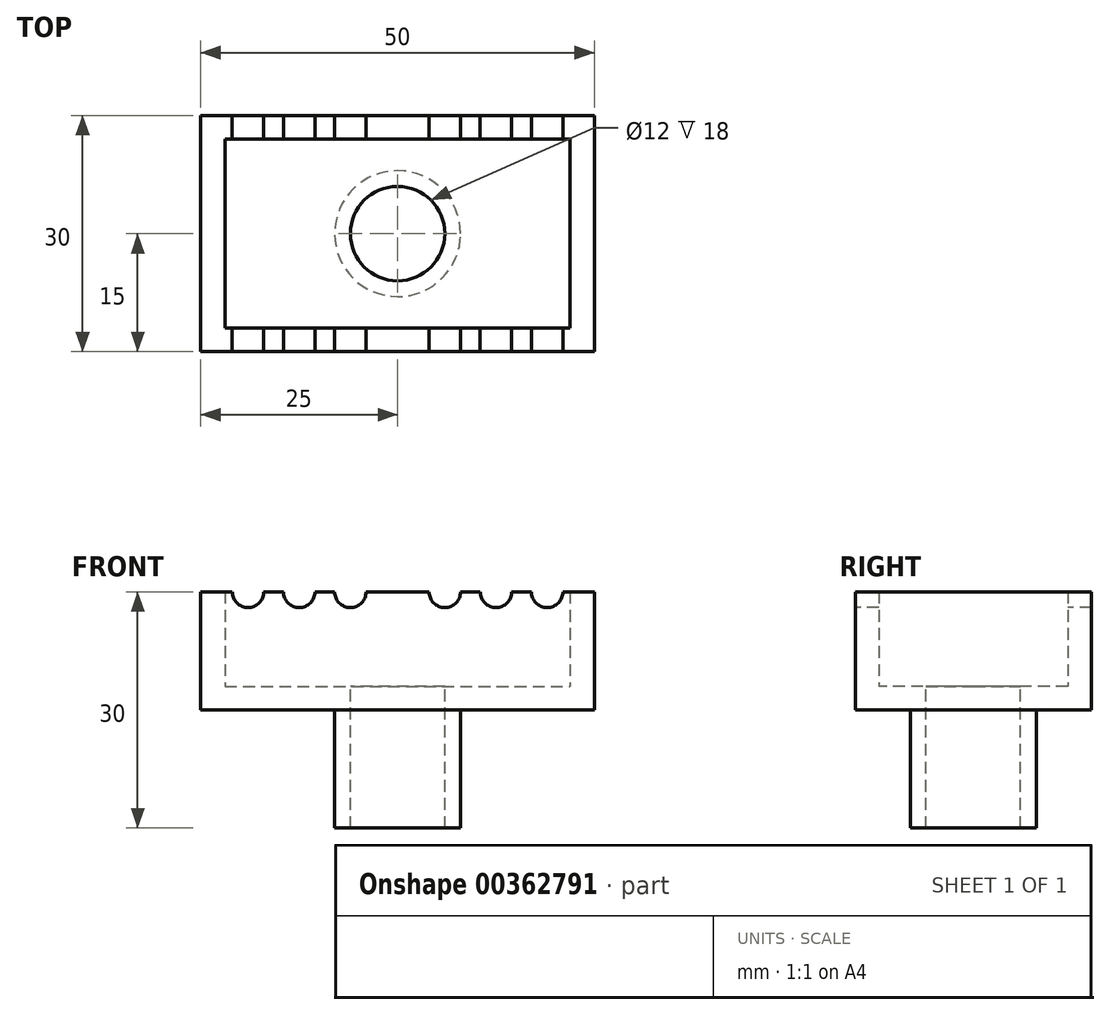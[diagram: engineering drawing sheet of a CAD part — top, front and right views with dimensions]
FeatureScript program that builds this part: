
annotation { "Feature Type Name" : "Feature", "Feature Type Description" : "" }
export const myFeature = defineFeature(function(context is Context, id is Id, definition is map)
    precondition{}
    {
        {
            var Q0;
            Q0=qCreatedBy(makeId("Top.planeOp"),FACE);
            var sketch = newSketch(context, id + "F0", { "sketchPlane" : qUnion([Q0])});
            skCircle(sketch, "E0", {"center": v(0, 0) * mm, "radius": 8 * mm});
            skCircle(sketch, "E1", {"center": v(0, 0) * mm, "radius": 6 * mm});
            skLineSegment(sketch, "E2.bottom", {"start": v(-25, 15) * mm, "end": v(25, 15) * mm});
            skLineSegment(sketch, "E2.top", {"start": v(-25, -15) * mm, "end": v(25, -15) * mm});
            skLineSegment(sketch, "E2.left", {"start": v(-25, 15) * mm, "end": v(-25, -15) * mm});
            skLineSegment(sketch, "E2.right", {"start": v(25, 15) * mm, "end": v(25, -15) * mm});
            skLineSegment(sketch, "E3.bottom", {"start": v(-21.93, 12) * mm, "end": v(21.93, 12) * mm});
            skLineSegment(sketch, "E3.top", {"start": v(-21.93, -12) * mm, "end": v(21.93, -12) * mm});
            skLineSegment(sketch, "E3.left", {"start": v(-21.93, 12) * mm, "end": v(-21.93, -12) * mm});
            skLineSegment(sketch, "E3.right", {"start": v(21.93, 12) * mm, "end": v(21.93, -12) * mm});
            skSolve(sketch);
        }
        {
            var Q0;
            Q0 = qSketchRegion(id + "F0", true);
            extrude(context, id + "F1", {"entities" : qUnion([Q0]), "depth" : 15 * mm});
        }
        {
            var Q0;
            Q0=makeQuery(id+"F0.imprint","IMPRINT",FACE,{"disambiguationData":[TD([[makeQuery(id+"F0.imprint","IMPRINT",EDGE,{"derivedFrom":sQuery(id+"F0.wireOp",EDGE,"E0")}),-1.0]])]});
            extrude(context, id + "F2", {"entities" : qUnion([Q0]), "operationType" : NewBodyOperationType.ADD, "depth" : 3 * mm});
        }
        {
            var Q0;
            Q0=makeQuery(id+"F0.imprint","IMPRINT",FACE,{"disambiguationData":[TD([[makeQuery(id+"F0.imprint","IMPRINT",EDGE,{"derivedFrom":sQuery(id+"F0.wireOp",EDGE,"E0")}),1.0]])]});
            extrude(context, id + "F3", {"entities" : qUnion([Q0]), "operationType" : NewBodyOperationType.ADD, "oppositeDirection" : true, "depth" : 15 * mm, "hasSecondDirection" : true, "secondDirectionOppositeDirection" : false, "secondDirectionDepth" : 3 * mm});
        }
        {
            var Q0;
            Q0=makeQuery(id+"F1.opExtrude","SWEPT_FACE",FACE,{"disambiguationData":[OSD([sQuery(id+"F0.wireOp",EDGE,"E2.top")])]});
            var sketch = newSketch(context, id + "F4", { "sketchPlane" : qUnion([Q0])});
            skLineSegment(sketch, "E4.0", {"start": v(-25, 15) * mm, "end": v(25, 15) * mm});
            skCircle(sketch, "E5", {"center": v(-19, 15) * mm, "radius": 2 * mm});
            skCircle(sketch, "E6", {"center": v(-6, 15) * mm, "radius": 2 * mm});
            skCircle(sketch, "E7", {"center": v(-12.5, 15) * mm, "radius": 2 * mm});
            skCircle(sketch, "E8.MirrorC", {"center": v(6, 15) * mm, "radius": 2 * mm});
            skCircle(sketch, "E9.MirrorC", {"center": v(12.5, 15) * mm, "radius": 2 * mm});
            skCircle(sketch, "E10.MirrorC", {"center": v(19, 15) * mm, "radius": 2 * mm});
            skSolve(sketch);
        }
        {
            var Q0;
            Q0 = qSketchRegion(id + "F4", true);
            extrude(context, id + "F5", {"entities" : qUnion([Q0]), "operationType" : NewBodyOperationType.REMOVE, "oppositeDirection" : true, "depth" : 46.6 * mm});
        }
    });
